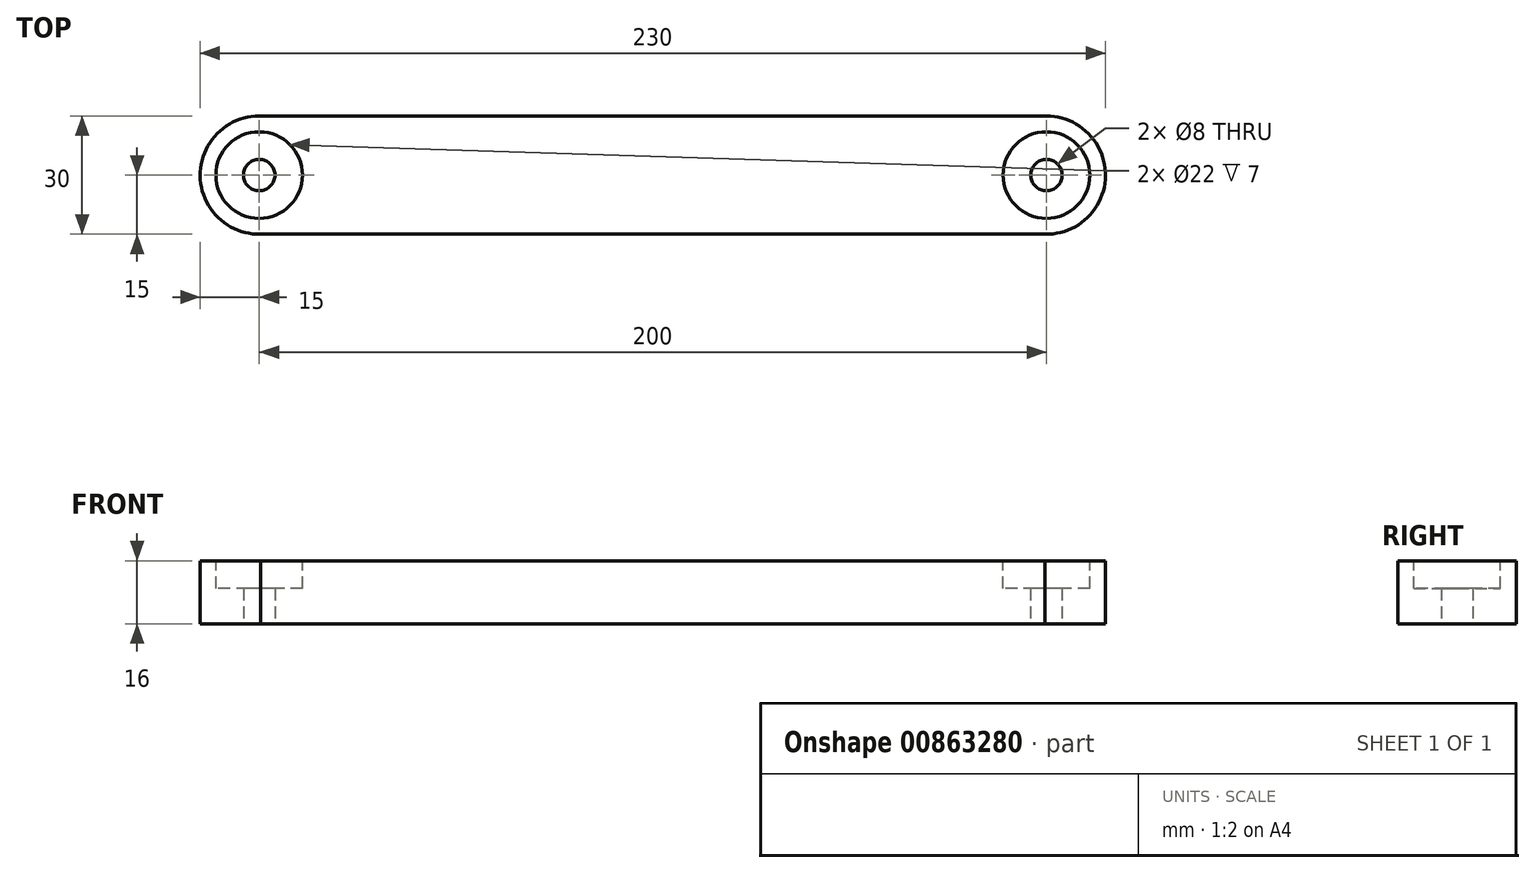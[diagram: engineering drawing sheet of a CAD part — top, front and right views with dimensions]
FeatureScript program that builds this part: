
annotation { "Feature Type Name" : "Feature", "Feature Type Description" : "" }
export const myFeature = defineFeature(function(context is Context, id is Id, definition is map)
    precondition{}
    {
        {
            var Q0;
            Q0=qCreatedBy(makeId("Top.planeOp"),FACE);
            var sketch = newSketch(context, id + "F0", { "sketchPlane" : qUnion([Q0])});
            skCircle(sketch, "E0", {"center": v(0, 0) * mm, "radius": 15 * mm});
            skCircle(sketch, "E1", {"center": v(200, 0) * mm, "radius": 15 * mm});
            skLineSegment(sketch, "E2", {"start": v(0, 0) * mm, "end": v(200, 0) * mm});
            skLineSegment(sketch, "E3", {"start": v(0, 15) * mm, "end": v(200, 15) * mm});
            skLineSegment(sketch, "E4", {"start": v(200.36, -15) * mm, "end": v(0.36, -15) * mm});
            skCircle(sketch, "E5", {"center": v(0, 0) * mm, "radius": 4 * mm});
            skCircle(sketch, "E6", {"center": v(200, 0) * mm, "radius": 4 * mm});
            skSolve(sketch);
        }
        {
            var Q0;
            Q0 = qSketchRegion(id + "F0", true);
            extrude(context, id + "F1", {"entities" : qUnion([Q0]), "depth" : 16 * mm, "offsetDistance" : 25 * mm});
        }
        {
            var Q0;
            Q0=makeQuery(id+"F1.opExtrude","CAP_FACE",FACE,{"disambiguationData":[OSD([sQuery(id+"F0.wireOp",EDGE,"E0"),sQuery(id+"F0.wireOp",EDGE,"E1"),sQuery(id+"F0.wireOp",EDGE,"E3"),sQuery(id+"F0.wireOp",EDGE,"E4"),sQuery(id+"F0.wireOp",EDGE,"E5"),sQuery(id+"F0.wireOp",EDGE,"E6")])],"isStart":false});
            var sketch = newSketch(context, id + "F2", { "sketchPlane" : qUnion([Q0])});
            skCircle(sketch, "E7", {"center": v(0, 0) * mm, "radius": 11 * mm});
            skCircle(sketch, "E8", {"center": v(200, 0) * mm, "radius": 11 * mm});
            skSolve(sketch);
        }
        {
            var Q0;
            Q0 = qSketchRegion(id + "F2", true);
            extrude(context, id + "F3", {"entities" : qUnion([Q0]), "operationType" : NewBodyOperationType.REMOVE, "oppositeDirection" : true, "depth" : 7 * mm, "offsetDistance" : 25 * mm});
        }
    });
